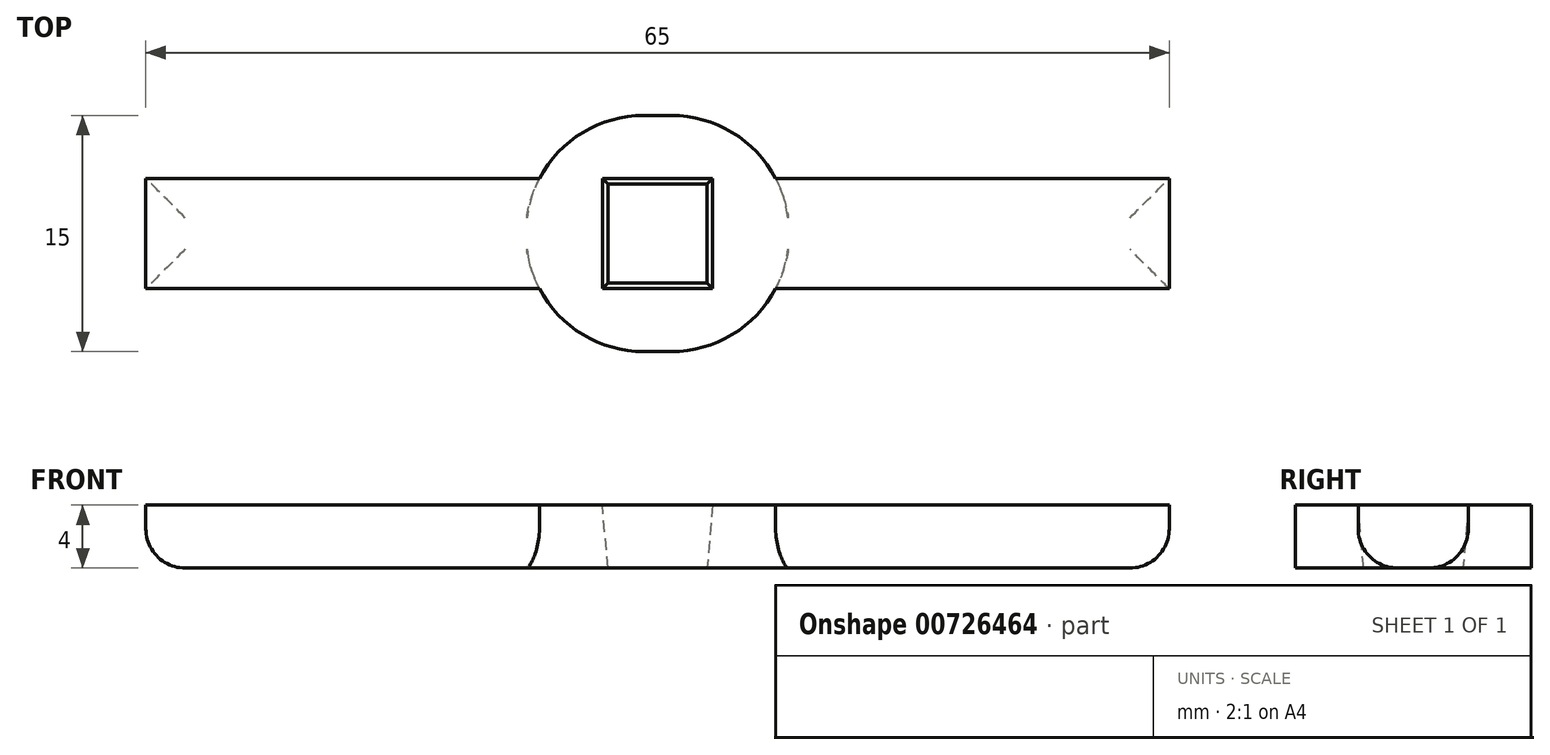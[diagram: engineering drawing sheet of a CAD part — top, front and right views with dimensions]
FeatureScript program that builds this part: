
annotation { "Feature Type Name" : "Feature", "Feature Type Description" : "" }
export const myFeature = defineFeature(function(context is Context, id is Id, definition is map)
    precondition{}
    {
        {
            var Q0;
            Q0=qCreatedBy(makeId("Top.planeOp"),FACE);
            var sketch = newSketch(context, id + "F0", { "sketchPlane" : qUnion([Q0])});
            skLineSegment(sketch, "E0.bottom", {"start": v(7.5, 7.5) * mm, "end": v(-7.5, 7.5) * mm});
            skLineSegment(sketch, "E0.top", {"start": v(7.5, -7.5) * mm, "end": v(-7.5, -7.5) * mm});
            skLineSegment(sketch, "E0.left", {"start": v(7.5, 7.5) * mm, "end": v(7.5, -7.5) * mm});
            skLineSegment(sketch, "E0.right", {"start": v(-7.5, 7.5) * mm, "end": v(-7.5, -7.5) * mm});
            skPoint(sketch, "E0.middle", {"position": v(0, 0) * mm});
            skLineSegment(sketch, "E1.bottom", {"start": v(3.5, 3.5) * mm, "end": v(-3.5, 3.5) * mm});
            skLineSegment(sketch, "E1.top", {"start": v(3.5, -3.5) * mm, "end": v(-3.5, -3.5) * mm});
            skLineSegment(sketch, "E1.left", {"start": v(3.5, 3.5) * mm, "end": v(3.5, -3.5) * mm});
            skLineSegment(sketch, "E1.right", {"start": v(-3.5, 3.5) * mm, "end": v(-3.5, -3.5) * mm});
            skSolve(sketch);
        }
        {
            var Q0;
            Q0 = qSketchRegion(id + "F0", true);
            var Q1;
            Q1=makeQuery(id+"F0.imprint","IMPRINT",FACE,{"disambiguationData":[TD([[makeQuery(id+"F0.imprint","IMPRINT",EDGE,{"derivedFrom":sQuery(id+"F0.wireOp",EDGE,"E1.bottom")}),1.0]])]});
            extrude(context, id + "F1", {"entities" : qUnion([Q0, Q1]), "depth" : 4 * mm, "offsetDistance" : 25 * mm});
        }
        {
            var Q0;
            Q0=makeQuery(id+"F1.opExtrude","CAP_FACE",FACE,{"disambiguationData":[OSD([sQuery(id+"F0.wireOp",EDGE,"E0.bottom"),sQuery(id+"F0.wireOp",EDGE,"E0.top"),sQuery(id+"F0.wireOp",EDGE,"E0.left"),sQuery(id+"F0.wireOp",EDGE,"E0.right")])],"isStart":false});
            var sketch = newSketch(context, id + "F2", { "sketchPlane" : qUnion([Q0])});
            skLineSegment(sketch, "E2.bottom", {"start": v(3.5, 3.5) * mm, "end": v(-3.5, 3.5) * mm});
            skLineSegment(sketch, "E2.top", {"start": v(3.5, -3.5) * mm, "end": v(-3.5, -3.5) * mm});
            skLineSegment(sketch, "E2.left", {"start": v(3.5, 3.5) * mm, "end": v(3.5, -3.5) * mm});
            skLineSegment(sketch, "E2.right", {"start": v(-3.5, 3.5) * mm, "end": v(-3.5, -3.5) * mm});
            skPoint(sketch, "E2.middle", {"position": v(0, 0) * mm});
            skSolve(sketch);
        }
        {
            var Q0;
            Q0 = qSketchRegion(id + "F2", true);
            extrude(context, id + "F3", {"entities" : qUnion([Q0]), "operationType" : NewBodyOperationType.REMOVE, "oppositeDirection" : true, "depth" : 4 * mm, "offsetDistance" : 25 * mm, "hasDraft" : true, "draftAngle" : 5 * degree, "draftPullDirection" : true});
        }
        {
            var Q0;
            Q0=makeQuery(id+"F1.opExtrude","SWEPT_FACE",FACE,{"disambiguationData":[OSD([sQuery(id+"F0.wireOp",EDGE,"E0.left")])]});
            var sketch = newSketch(context, id + "F4", { "sketchPlane" : qUnion([Q0])});
            skLineSegment(sketch, "E3.bottom", {"start": v(3.5, 4) * mm, "end": v(-3.5, 4) * mm});
            skLineSegment(sketch, "E3.top", {"start": v(3.5, 0) * mm, "end": v(-3.5, 0) * mm});
            skLineSegment(sketch, "E3.left", {"start": v(3.5, 4) * mm, "end": v(3.5, 0) * mm});
            skLineSegment(sketch, "E3.right", {"start": v(-3.5, 4) * mm, "end": v(-3.5, 0) * mm});
            skPoint(sketch, "E3.middle", {"position": v(0, 2) * mm});
            skPoint(sketch, "E3.middle.positionSnap0", {"position": v(7.5, 2) * mm});
            skPoint(sketch, "E3.centerSnap0", {"position": v(7.5, 2) * mm});
            skSolve(sketch);
        }
        {
            var Q0;
            Q0 = qSketchRegion(id + "F4", true);
            extrude(context, id + "F5", {"entities" : qUnion([Q0]), "operationType" : NewBodyOperationType.ADD, "depth" : 25 * mm, "offsetDistance" : 25 * mm});
        }
        {
            var Q0;
            Q0=makeQuery(id+"F1.opExtrude","SWEPT_FACE",FACE,{"disambiguationData":[OSD([sQuery(id+"F0.wireOp",EDGE,"E0.right")])]});
            var sketch = newSketch(context, id + "F6", { "sketchPlane" : qUnion([Q0])});
            skLineSegment(sketch, "E4.bottom", {"start": v(3.5, 4) * mm, "end": v(-3.5, 4) * mm});
            skLineSegment(sketch, "E4.top", {"start": v(3.5, 0) * mm, "end": v(-3.5, 0) * mm});
            skLineSegment(sketch, "E4.left", {"start": v(3.5, 4) * mm, "end": v(3.5, 0) * mm});
            skLineSegment(sketch, "E4.right", {"start": v(-3.5, 4) * mm, "end": v(-3.5, 0) * mm});
            skPoint(sketch, "E4.middle", {"position": v(0, 2) * mm});
            skPoint(sketch, "E4.middle.positionSnap0", {"position": v(7.5, 2) * mm});
            skPoint(sketch, "E4.centerSnap0", {"position": v(7.5, 2) * mm});
            skSolve(sketch);
        }
        {
            var Q0;
            Q0 = qSketchRegion(id + "F6", true);
            extrude(context, id + "F7", {"entities" : qUnion([Q0]), "operationType" : NewBodyOperationType.ADD, "depth" : 25 * mm, "offsetDistance" : 25 * mm});
        }
        {
            var Q0;
            Q0=makeQuery(id+"F1.opExtrude","SWEPT_EDGE",EDGE,{"disambiguationData":[OSD([sQuery(id+"F0.wireOp",EDGE,"E0.bottom"),sQuery(id+"F0.wireOp",EDGE,"E0.right")])]});
            var Q1;
            Q1=makeQuery(id+"F1.opExtrude","SWEPT_EDGE",EDGE,{"disambiguationData":[OSD([sQuery(id+"F0.wireOp",EDGE,"E0.bottom"),sQuery(id+"F0.wireOp",EDGE,"E0.left")])]});
            var Q2;
            Q2=makeQuery(id+"F1.opExtrude","SWEPT_EDGE",EDGE,{"disambiguationData":[OSD([sQuery(id+"F0.wireOp",EDGE,"E0.top"),sQuery(id+"F0.wireOp",EDGE,"E0.left")])]});
            var Q3;
            Q3=makeQuery(id+"F1.opExtrude","SWEPT_EDGE",EDGE,{"disambiguationData":[OSD([sQuery(id+"F0.wireOp",EDGE,"E0.top"),sQuery(id+"F0.wireOp",EDGE,"E0.right")])]});
            fillet(context, id + "F8", {"entities" : qUnion([Q0, Q1, Q2, Q3]), "radius" : 7.5 * mm, "tangentPropagation" : true, "allowEdgeOverflow" : false});
        }
        {
            var Q0;
            Q0=makeQuery(id+"F7.opExtrude","CAP_EDGE",EDGE,{"disambiguationData":[OSD([sQuery(id+"F6.wireOp",EDGE,"E4.top")])],"isStart":false});
            var Q1;
            Q1=makeQuery(id+"F7.opExtrude","SWEPT_EDGE",EDGE,{"disambiguationData":[OSD([sQuery(id+"F0.wireOp",EDGE,"E0.right"),sQuery(id+"F6.wireOp",EDGE,"E4.top"),sQuery(id+"F6.wireOp",EDGE,"E4.left")])]});
            var Q2;
            Q2=makeQuery(id+"F7.opExtrude","SWEPT_EDGE",EDGE,{"disambiguationData":[OSD([sQuery(id+"F0.wireOp",EDGE,"E0.right"),sQuery(id+"F6.wireOp",EDGE,"E4.top"),sQuery(id+"F6.wireOp",EDGE,"E4.right")])]});
            var Q3;
            Q3=makeQuery(id+"F5.opExtrude","SWEPT_EDGE",EDGE,{"disambiguationData":[OSD([sQuery(id+"F0.wireOp",EDGE,"E0.left"),sQuery(id+"F4.wireOp",EDGE,"E3.top"),sQuery(id+"F4.wireOp",EDGE,"E3.left")])]});
            var Q4;
            Q4=makeQuery(id+"F5.opExtrude","CAP_EDGE",EDGE,{"disambiguationData":[OSD([sQuery(id+"F4.wireOp",EDGE,"E3.top")])],"isStart":false});
            var Q5;
            Q5=makeQuery(id+"F5.opExtrude","SWEPT_EDGE",EDGE,{"disambiguationData":[OSD([sQuery(id+"F0.wireOp",EDGE,"E0.left"),sQuery(id+"F4.wireOp",EDGE,"E3.top"),sQuery(id+"F4.wireOp",EDGE,"E3.right")])]});
            fillet(context, id + "F9", {"entities" : qUnion([Q0, Q1, Q2, Q3, Q4, Q5]), "radius" : 2.5 * mm, "tangentPropagation" : true, "allowEdgeOverflow" : false});
        }
    });
